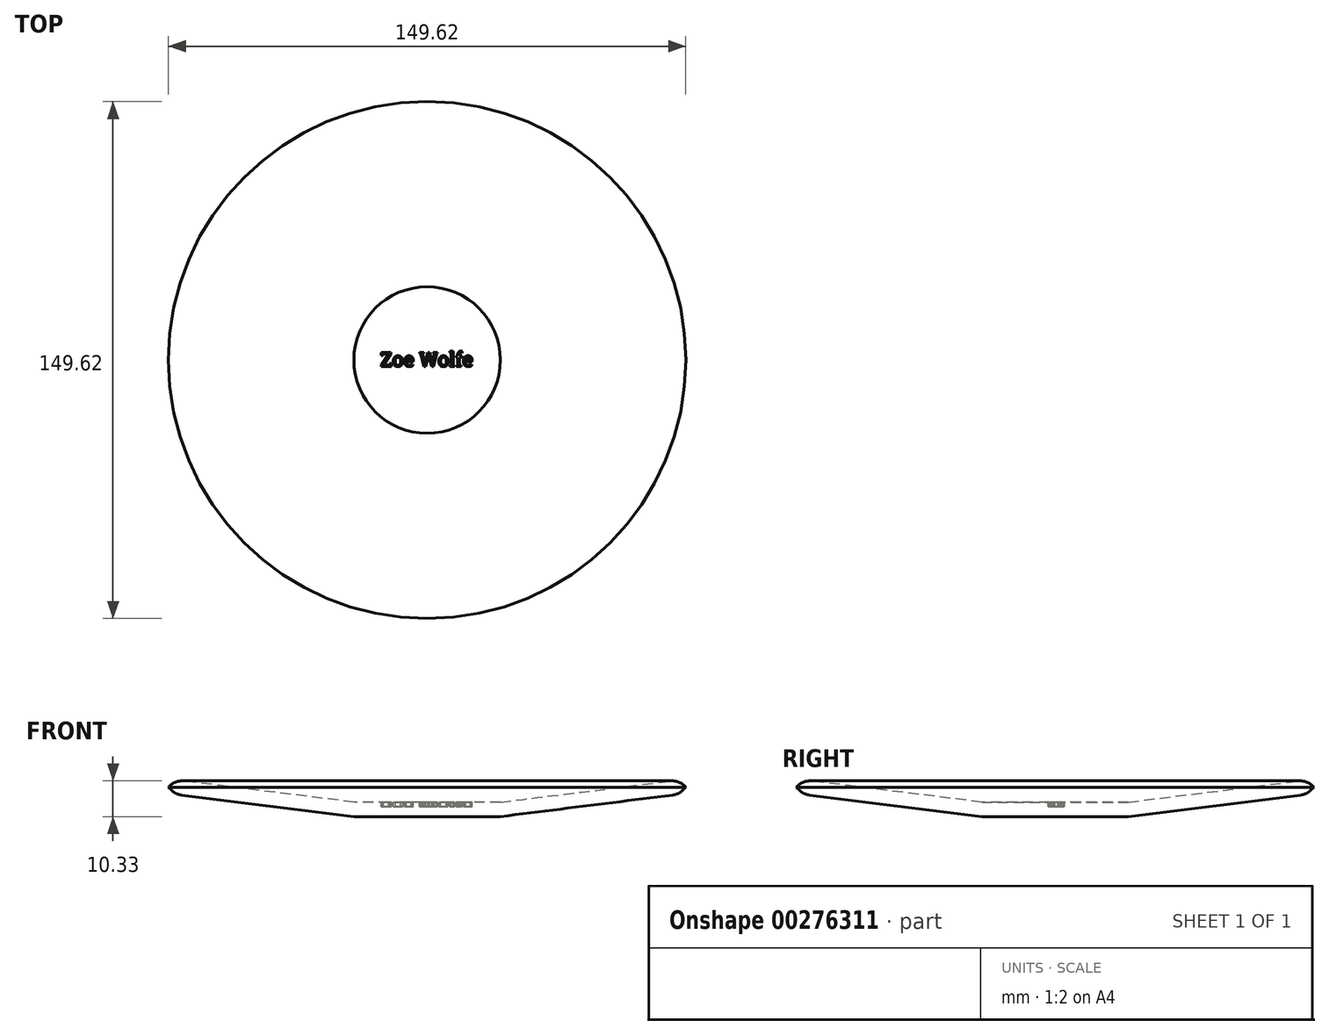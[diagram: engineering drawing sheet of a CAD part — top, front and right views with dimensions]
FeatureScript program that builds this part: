
annotation { "Feature Type Name" : "Feature", "Feature Type Description" : "" }
export const myFeature = defineFeature(function(context is Context, id is Id, definition is map)
    precondition{}
    {
        {
            var Q0;
            Q0=qCreatedBy(makeId("Front.planeOp"),FACE);
            var sketch = newSketch(context, id + "F0", { "sketchPlane" : qUnion([Q0])});
            skLineSegment(sketch, "E0", {"start": v(0, 0) * mm, "end": v(-21.2, 0) * mm});
            skLineSegment(sketch, "E1", {"start": v(-21.2, 0) * mm, "end": v(-72.74, 6.44) * mm});
            skLineSegment(sketch, "E2", {"start": v(-72.74, 6.44) * mm, "end": v(-74.81, 8.52) * mm});
            skLineSegment(sketch, "E3", {"start": v(-74.81, 8.52) * mm, "end": v(-72.74, 10.6) * mm});
            skLineSegment(sketch, "E4", {"start": v(-72.74, 10.6) * mm, "end": v(-21.2, 4.16) * mm});
            skLineSegment(sketch, "E5", {"start": v(-21.2, 4.16) * mm, "end": v(0, 4.16) * mm});
            skLineSegment(sketch, "E6", {"start": v(0, 4.16) * mm, "end": v(0, 0) * mm});
            skSolve(sketch);
        }
        {
            var Q0;
            Q0=makeQuery(id+"F0.imprint","IMPRINT",FACE,{"disambiguationData":[TD([[makeQuery(id+"F0.imprint","IMPRINT",EDGE,{"derivedFrom":sQuery(id+"F0.wireOp",EDGE,"E0")}),-1.0]])]});
            var Q1;
            Q1=sQuery(id+"F0.wireOp",EDGE,"E6");
            revolve(context, id + "F1", {"entities" : qUnion([Q0]), "axis" : qUnion([Q1]), "revolveType" : RevolveType.FULL});
        }
        {
            var Q0;
            Q0=makeQuery(id+"F1.opRevolve","SWEPT_EDGE",EDGE,{"disambiguationData":[OSD([sQuery(id+"F0.wireOp",EDGE,"E3"),sQuery(id+"F0.wireOp",EDGE,"E4")])]});
            var Q1;
            Q1=makeQuery(id+"F1.opRevolve","SWEPT_EDGE",EDGE,{"disambiguationData":[OSD([sQuery(id+"F0.wireOp",EDGE,"E1"),sQuery(id+"F0.wireOp",EDGE,"E2")])]});
            fillet(context, id + "F2", {"entities" : qUnion([Q0, Q1]), "radius" : 5.08 * mm, "tangentPropagation" : true, "allowEdgeOverflow" : false});
        }
        {
            var Q0;
            Q0=makeQuery(id+"F1.opRevolve","SWEPT_FACE",FACE,{"disambiguationData":[OSD([sQuery(id+"F0.wireOp",EDGE,"E5")])]});
            var sketch = newSketch(context, id + "F3", { "sketchPlane" : qUnion([Q0])});
            skText(sketch, "E7", { "text": "Zoe Wolfe ", "fontName": "RobotoSlab-Regular.ttf"});
            const initialGuessF3  = {"E7": [-0.0135, -0.00187, 1, 0, 0.00416]};
            skSetInitialGuess(sketch, initialGuessF3);
            skSolve(sketch);
        }
        {
            var Q0;
            Q0 = qSketchRegion(id + "F3", true);
            extrude(context, id + "F4", {"entities" : qUnion([Q0]), "operationType" : NewBodyOperationType.REMOVE, "oppositeDirection" : true, "depth" : 1.27 * mm});
        }
    });
